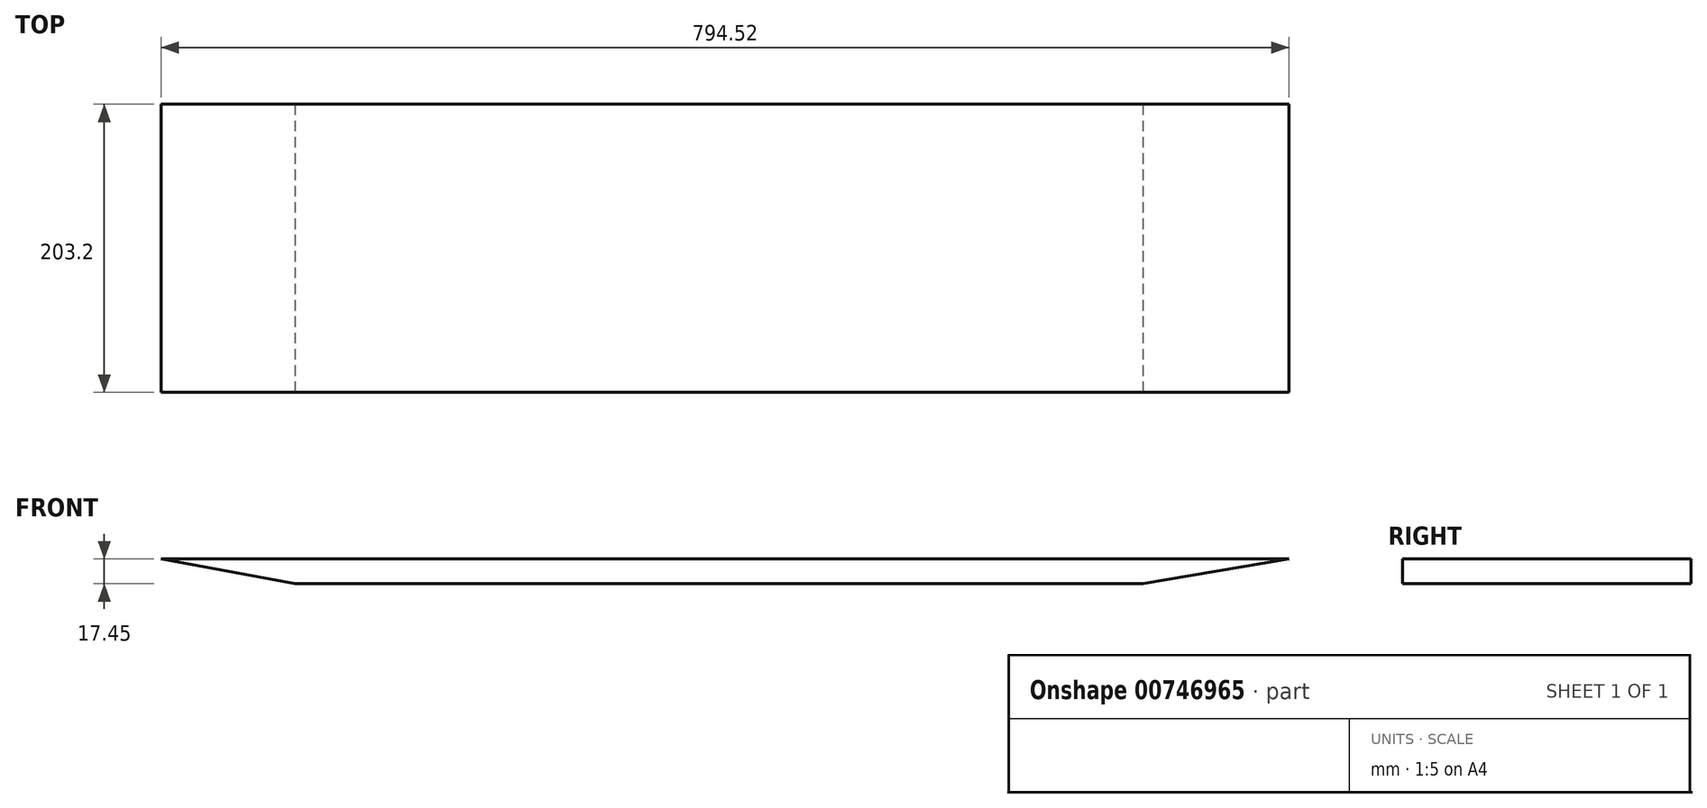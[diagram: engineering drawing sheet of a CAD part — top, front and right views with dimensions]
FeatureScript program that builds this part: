
annotation { "Feature Type Name" : "Feature", "Feature Type Description" : "" }
export const myFeature = defineFeature(function(context is Context, id is Id, definition is map)
    precondition{}
    {
        {
            var Q0;
            Q0=qCreatedBy(makeId("Front.planeOp"),FACE);
            var sketch = newSketch(context, id + "F0", { "sketchPlane" : qUnion([Q0])});
            skLineSegment(sketch, "E0", {"start": v(0, 0) * mm, "end": v(800.1, 0) * mm});
            skLineSegment(sketch, "E1", {"start": v(800.1, 0) * mm, "end": v(800.1, 17.45) * mm});
            skLineSegment(sketch, "E2", {"start": v(800.1, 17.45) * mm, "end": v(0, 17.45) * mm});
            skLineSegment(sketch, "E3", {"start": v(0, 17.45) * mm, "end": v(0, 0) * mm});
            skSolve(sketch);
        }
        {
            var Q0;
            Q0=makeQuery(id+"F0.imprint","IMPRINT",FACE,{"disambiguationData":[TD([[makeQuery(id+"F0.imprint","IMPRINT",EDGE,{"derivedFrom":sQuery(id+"F0.wireOp",EDGE,"E0")}),1.0]])]});
            extrude(context, id + "F1", {"entities" : qUnion([Q0]), "oppositeDirection" : true, "depth" : 203.2 * mm, "offsetDistance" : 25.4 * mm});
        }
        {
            var Q0;
            Q0=qCreatedBy(makeId("Front.planeOp"),FACE);
            var sketch = newSketch(context, id + "F2", { "sketchPlane" : qUnion([Q0])});
            skLineSegment(sketch, "E4", {"start": v(0, 0) * mm, "end": v(99.82, 0) * mm});
            skLineSegment(sketch, "E5", {"start": v(99.82, 0) * mm, "end": v(0, 18.48) * mm});
            skLineSegment(sketch, "E6", {"start": v(0, 18.48) * mm, "end": v(0, 0) * mm});
            skSolve(sketch);
        }
        {
            var Q0;
            Q0=makeQuery(id+"F2.imprint","IMPRINT",FACE,{"disambiguationData":[TD([[makeQuery(id+"F2.imprint","IMPRINT",EDGE,{"derivedFrom":sQuery(id+"F2.wireOp",EDGE,"E4")}),1.0]])]});
            extrude(context, id + "F3", {"entities" : qUnion([Q0]), "operationType" : NewBodyOperationType.REMOVE, "oppositeDirection" : true, "depth" : 203.2 * mm, "offsetDistance" : 25.4 * mm});
        }
        {
            var Q0;
            Q0=makeQuery(id+"F1.opExtrude","CAP_FACE",FACE,{"disambiguationData":[OSD([sQuery(id+"F0.wireOp",EDGE,"E0"),sQuery(id+"F0.wireOp",EDGE,"E1"),sQuery(id+"F0.wireOp",EDGE,"E2"),sQuery(id+"F0.wireOp",EDGE,"E3")])],"isStart":true});
            var sketch = newSketch(context, id + "F4", { "sketchPlane" : qUnion([Q0])});
            skLineSegment(sketch, "E7", {"start": v(697.02, 0) * mm, "end": v(800.1, 0) * mm});
            skLineSegment(sketch, "E8", {"start": v(800.1, 0) * mm, "end": v(800.1, 17.45) * mm});
            skLineSegment(sketch, "E9", {"start": v(800.1, 17.45) * mm, "end": v(697.02, 0) * mm});
            skSolve(sketch);
        }
        {
            var Q0;
            Q0=makeQuery(id+"F4.imprint","IMPRINT",FACE,{"disambiguationData":[TD([[makeQuery(id+"F4.imprint","IMPRINT",EDGE,{"derivedFrom":sQuery(id+"F4.wireOp",EDGE,"E7")}),1.0]])]});
            extrude(context, id + "F5", {"entities" : qUnion([Q0]), "operationType" : NewBodyOperationType.REMOVE, "oppositeDirection" : true, "depth" : 203.2 * mm, "offsetDistance" : 25.4 * mm});
        }
    });
